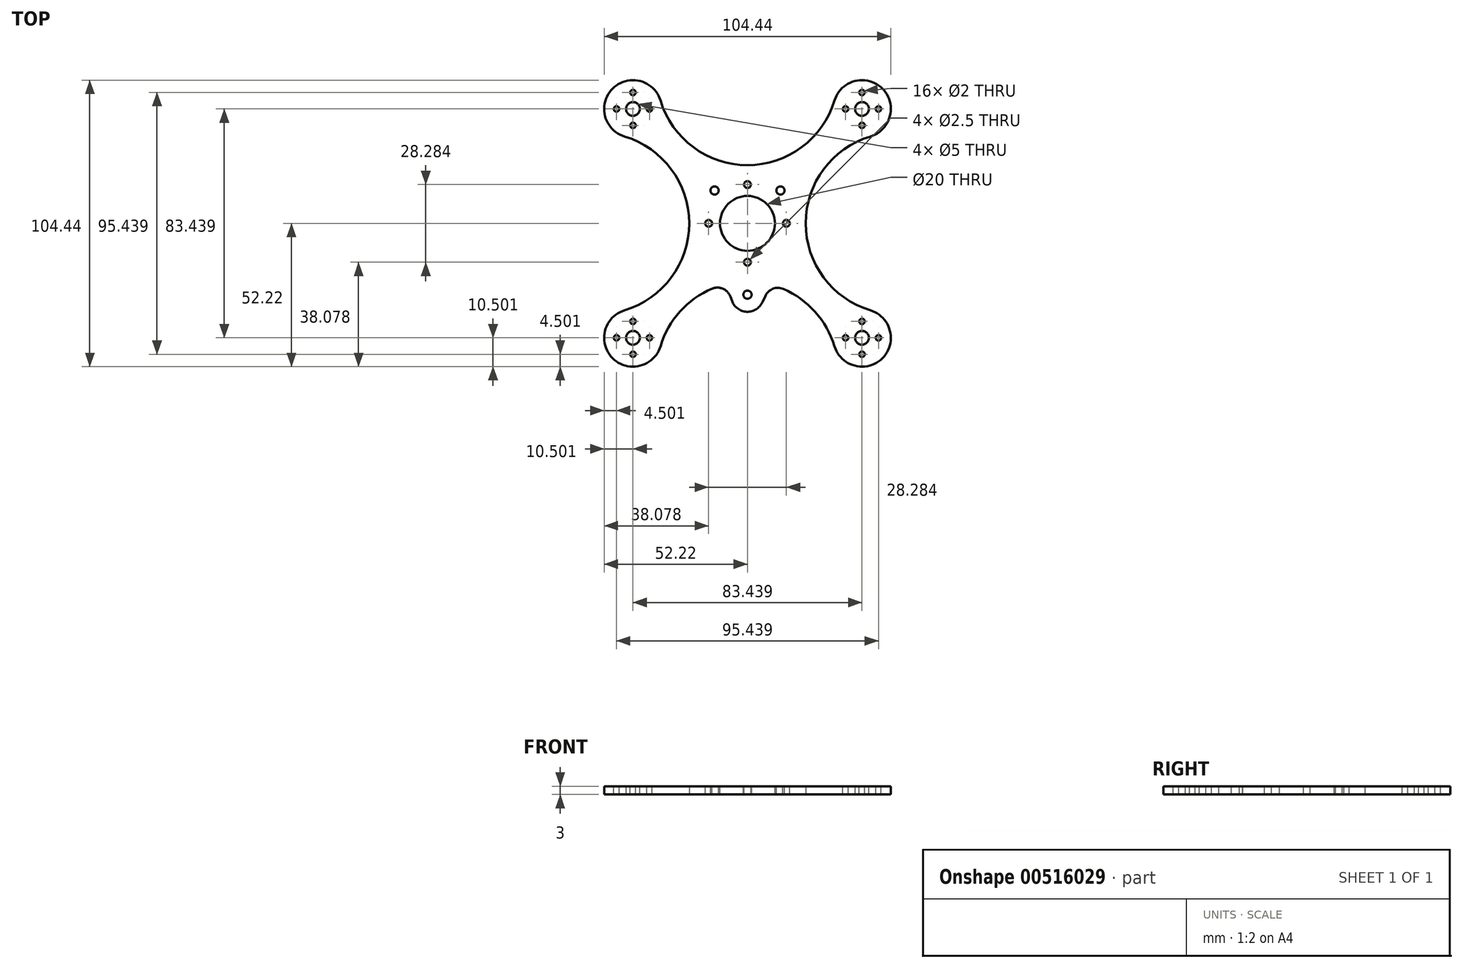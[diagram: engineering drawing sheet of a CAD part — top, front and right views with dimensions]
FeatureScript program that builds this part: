
annotation { "Feature Type Name" : "Feature", "Feature Type Description" : "" }
export const myFeature = defineFeature(function(context is Context, id is Id, definition is map)
    precondition{}
    {
        {
            var Q0;
            Q0=qCreatedBy(makeId("Top.planeOp"),FACE);
            var sketch = newSketch(context, id + "F0", { "sketchPlane" : qUnion([Q0])});
            skCircle(sketch, "E0", {"center": v(-41.72, 41.72) * mm, "radius": 38.5 * mm, "construction": true});
            skLineSegment(sketch, "E1", {"start": v(-41.72, 41.72) * mm, "end": v(41.72, 41.72) * mm, "construction": true});
            skLineSegment(sketch, "E2", {"start": v(41.72, -41.72) * mm, "end": v(-41.72, -41.72) * mm, "construction": true});
            skLineSegment(sketch, "E3", {"start": v(-41.72, -41.72) * mm, "end": v(-41.72, 41.72) * mm, "construction": true});
            skLineSegment(sketch, "E4", {"start": v(41.72, 41.72) * mm, "end": v(41.72, -41.72) * mm, "construction": true});
            skCircle(sketch, "E5", {"center": v(41.72, 41.72) * mm, "radius": 38.5 * mm, "construction": true});
            skCircle(sketch, "E6", {"center": v(41.72, -41.72) * mm, "radius": 38.5 * mm, "construction": true});
            skCircle(sketch, "E7", {"center": v(-41.72, -41.72) * mm, "radius": 38.5 * mm, "construction": true});
            skArc(sketch, "E8", {"start": v(31.67, -44.75) * mm, "mid": v(49.14, -49.14) * mm, "end": v(44.75, -31.67) * mm});
            skLineSegment(sketch, "E9", {"start": v(-41.72, 41.72) * mm, "end": v(41.72, -41.72) * mm, "construction": true});
            skLineSegment(sketch, "E10", {"start": v(-21.21, 0) * mm, "end": v(0, -21.21) * mm, "construction": true});
            skLineSegment(sketch, "E11", {"start": v(0, -21.21) * mm, "end": v(21.21, 0) * mm, "construction": true});
            skLineSegment(sketch, "E12", {"start": v(21.21, 0) * mm, "end": v(0, 21.21) * mm, "construction": true});
            skLineSegment(sketch, "E13", {"start": v(0, 21.21) * mm, "end": v(-21.21, 0) * mm, "construction": true});
            skArc(sketch, "E14", {"start": v(31.67, -44.75) * mm, "mid": v(22.99, -30.5) * mm, "end": v(8.47, -22.32) * mm});
            skArc(sketch, "E15", {"start": v(-44.75, -31.67) * mm, "mid": v(-21.21, 0) * mm, "end": v(-44.75, 31.67) * mm});
            skArc(sketch, "E16", {"start": v(-31.67, 44.75) * mm, "mid": v(0, 21.21) * mm, "end": v(31.67, 44.75) * mm});
            skArc(sketch, "E17", {"start": v(44.75, 31.67) * mm, "mid": v(21.21, 0) * mm, "end": v(44.75, -31.67) * mm});
            skArc(sketch, "E18.trimOffspring", {"start": v(-31.67, 44.75) * mm, "mid": v(-49.14, 49.14) * mm, "end": v(-44.75, 31.67) * mm});
            skArc(sketch, "E19.trimOffspring", {"start": v(44.75, 31.67) * mm, "mid": v(49.14, 49.14) * mm, "end": v(31.67, 44.75) * mm});
            skArc(sketch, "E20.trimOffspring", {"start": v(-44.75, -31.67) * mm, "mid": v(-49.14, -49.14) * mm, "end": v(-31.67, -44.75) * mm});
            skArc(sketch, "E21", {"start": v(-5.63, -28.3) * mm, "mid": v(0, -32.22) * mm, "end": v(5.63, -28.3) * mm});
            skLineSegment(sketch, "E22", {"start": v(-5.63, -28.3) * mm, "end": v(-7.91, -22.17) * mm});
            skLineSegment(sketch, "E23", {"start": v(8.47, -22.32) * mm, "end": v(5.44, -28.77) * mm});
            skArc(sketch, "E24.trimOffspring", {"start": v(-7.91, -22.17) * mm, "mid": v(-22.78, -30.31) * mm, "end": v(-31.67, -44.75) * mm});
            skSolve(sketch);
        }
        {
            var Q0;
            Q0 = qSketchRegion(id + "F0", true);
            extrude(context, id + "F1", {"entities" : qUnion([Q0]), "depth" : 3 * mm, "offsetDistance" : 25 * mm});
        }
        {
            var Q0;
            Q0=makeQuery(id+"F1.opExtrude","CAP_FACE",FACE,{"disambiguationData":[OSD([sQuery(id+"F0.wireOp",EDGE,"E8"),sQuery(id+"F0.wireOp",EDGE,"E14"),sQuery(id+"F0.wireOp",EDGE,"E15"),sQuery(id+"F0.wireOp",EDGE,"E16"),sQuery(id+"F0.wireOp",EDGE,"E17"),sQuery(id+"F0.wireOp",EDGE,"E18.trimOffspring"),sQuery(id+"F0.wireOp",EDGE,"E19.trimOffspring"),sQuery(id+"F0.wireOp",EDGE,"E20.trimOffspring")])],"isStart":false});
            var sketch = newSketch(context, id + "F2", { "sketchPlane" : qUnion([Q0])});
            skCircle(sketch, "E25", {"center": v(0, -14.14) * mm, "radius": 1.25 * mm});
            skCircle(sketch, "E26", {"center": v(-14.14, 0) * mm, "radius": 1.25 * mm});
            skCircle(sketch, "E27", {"center": v(0, 14.14) * mm, "radius": 1.25 * mm});
            skCircle(sketch, "E28", {"center": v(14.14, 0) * mm, "radius": 1.25 * mm});
            skCircle(sketch, "E29", {"center": v(0, 0) * mm, "radius": 14.14 * mm, "construction": true});
            skCircle(sketch, "E30", {"center": v(-41.72, -41.72) * mm, "radius": 2.5 * mm});
            skCircle(sketch, "E31", {"center": v(41.72, -41.72) * mm, "radius": 2.5 * mm});
            skCircle(sketch, "E32", {"center": v(41.72, 41.72) * mm, "radius": 2.5 * mm});
            skCircle(sketch, "E33", {"center": v(-41.72, 41.72) * mm, "radius": 2.5 * mm});
            skCircle(sketch, "E34", {"center": v(-41.72, -41.72) * mm, "radius": 6 * mm, "construction": true});
            skCircle(sketch, "E35", {"center": v(41.72, -41.72) * mm, "radius": 6 * mm, "construction": true});
            skCircle(sketch, "E36", {"center": v(41.72, 41.72) * mm, "radius": 6 * mm, "construction": true});
            skCircle(sketch, "E37", {"center": v(-41.72, 41.72) * mm, "radius": 6 * mm, "construction": true});
            skCircle(sketch, "E38", {"center": v(-35.72, 41.72) * mm, "radius": 1 * mm});
            skCircle(sketch, "E39", {"center": v(-41.72, 35.72) * mm, "radius": 1 * mm});
            skCircle(sketch, "E40", {"center": v(-47.72, 41.72) * mm, "radius": 1 * mm});
            skCircle(sketch, "E41", {"center": v(-41.72, 47.72) * mm, "radius": 1 * mm});
            skCircle(sketch, "E42", {"center": v(35.72, 41.72) * mm, "radius": 1 * mm});
            skCircle(sketch, "E43", {"center": v(47.72, 41.72) * mm, "radius": 1 * mm});
            skCircle(sketch, "E44", {"center": v(41.72, 47.72) * mm, "radius": 1 * mm});
            skCircle(sketch, "E45", {"center": v(41.72, 35.72) * mm, "radius": 1 * mm});
            skCircle(sketch, "E46", {"center": v(41.72, -35.72) * mm, "radius": 1 * mm});
            skCircle(sketch, "E47", {"center": v(35.72, -41.72) * mm, "radius": 1 * mm});
            skCircle(sketch, "E48", {"center": v(41.72, -47.72) * mm, "radius": 1 * mm});
            skCircle(sketch, "E49", {"center": v(47.72, -41.72) * mm, "radius": 1 * mm});
            skCircle(sketch, "E50", {"center": v(-47.72, -41.72) * mm, "radius": 1 * mm});
            skCircle(sketch, "E51", {"center": v(-41.72, -47.72) * mm, "radius": 1 * mm});
            skCircle(sketch, "E52", {"center": v(-35.72, -41.72) * mm, "radius": 1 * mm});
            skCircle(sketch, "E53", {"center": v(-41.72, -35.72) * mm, "radius": 1 * mm});
            skCircle(sketch, "E54", {"center": v(0, 0) * mm, "radius": 10 * mm});
            skCircle(sketch, "E55", {"center": v(-12, 12) * mm, "radius": 1.5 * mm});
            skCircle(sketch, "E56", {"center": v(0, 0) * mm, "radius": 16.97 * mm, "construction": true});
            skCircle(sketch, "E57", {"center": v(12, 12) * mm, "radius": 1.5 * mm});
            skLineSegment(sketch, "E58", {"start": v(-12, -12) * mm, "end": v(12, 12) * mm, "construction": true});
            skCircle(sketch, "E59", {"center": v(0, -26) * mm, "radius": 1.5 * mm});
            skSolve(sketch);
        }
        {
            var Q0;
            Q0 = qSketchRegion(id + "F2", true);
            extrude(context, id + "F3", {"entities" : qUnion([Q0]), "operationType" : NewBodyOperationType.REMOVE, "endBound" : BoundingType.THROUGH_ALL, "oppositeDirection" : true, "depth" : 25 * mm, "offsetDistance" : 25 * mm});
        }
        {
            var Q0;
            Q0=makeQuery(id+"F1.opExtrude","SWEPT_EDGE",EDGE,{"disambiguationData":[OSD([sQuery(id+"F0.wireOp",EDGE,"E22"),sQuery(id+"F0.wireOp",EDGE,"E24.trimOffspring")])]});
            var Q1;
            Q1=makeQuery(id+"F1.opExtrude","SWEPT_EDGE",EDGE,{"disambiguationData":[OSD([sQuery(id+"F0.wireOp",EDGE,"E14"),sQuery(id+"F0.wireOp",EDGE,"E23")])]});
            fillet(context, id + "F4", {"entities" : qUnion([Q0, Q1]), "radius" : 5 * mm, "tangentPropagation" : true, "allowEdgeOverflow" : false});
        }
    });
